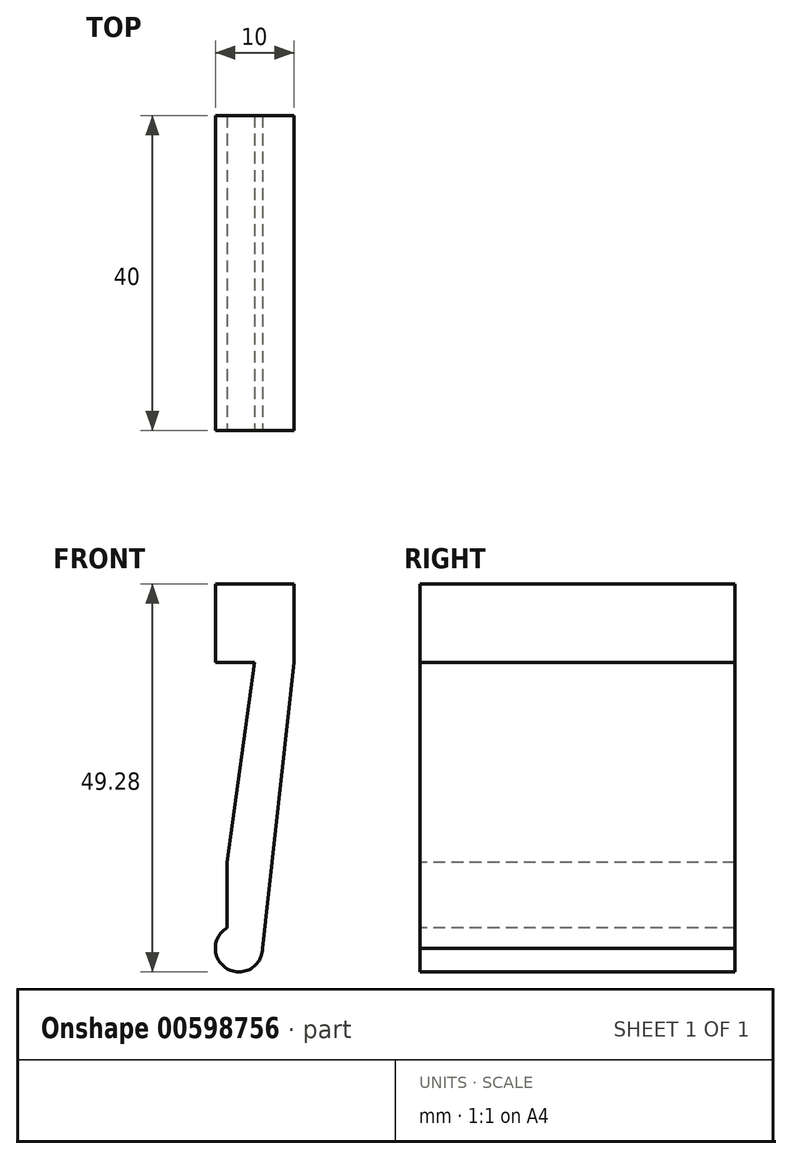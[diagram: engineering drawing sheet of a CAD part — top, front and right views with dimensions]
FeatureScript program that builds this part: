
annotation { "Feature Type Name" : "Feature", "Feature Type Description" : "" }
export const myFeature = defineFeature(function(context is Context, id is Id, definition is map)
    precondition{}
    {
        {
            var Q0;
            Q0=qCreatedBy(makeId("Front.planeOp"),FACE);
            var sketch = newSketch(context, id + "F0", { "sketchPlane" : qUnion([Q0])});
            skLineSegment(sketch, "E0.bottom", {"start": v(-5, 24.64) * mm, "end": v(5, 24.64) * mm});
            skLineSegment(sketch, "E0.top", {"start": v(-5, -24.64) * mm, "end": v(5, -24.64) * mm});
            skLineSegment(sketch, "E0.left", {"start": v(-5, 24.64) * mm, "end": v(-5, -24.64) * mm});
            skLineSegment(sketch, "E0.right", {"start": v(5, 24.64) * mm, "end": v(5, -24.64) * mm});
            skPoint(sketch, "E0.middle", {"position": v(0, 0) * mm});
            skSolve(sketch);
        }
        {
            var Q0;
            Q0=makeQuery(id+"F0.imprint","IMPRINT",FACE,{"disambiguationData":[TD([[makeQuery(id+"F0.imprint","IMPRINT",EDGE,{"derivedFrom":sQuery(id+"F0.wireOp",EDGE,"E0.bottom")}),-1.0]])]});
            extrude(context, id + "F1", {"entities" : qUnion([Q0]), "depth" : 40 * mm, "offsetDistance" : 25 * mm});
        }
        {
            var Q0;
            Q0=makeQuery(id+"F1.opExtrude","CAP_FACE",FACE,{"disambiguationData":[OSD([sQuery(id+"F0.wireOp",EDGE,"E0.bottom"),sQuery(id+"F0.wireOp",EDGE,"E0.top"),sQuery(id+"F0.wireOp",EDGE,"E0.left"),sQuery(id+"F0.wireOp",EDGE,"E0.right")])],"isStart":false});
            var sketch = newSketch(context, id + "F2", { "sketchPlane" : qUnion([Q0])});
            skLineSegment(sketch, "E1", {"start": v(-5, 24.64) * mm, "end": v(-5, 14.64) * mm});
            skFitSpline(sketch, "E2", {"points": [v(-5, 14.64) * mm, v(-5, -24.64) * mm], "startDerivative": vector(0, -39.28) * mm, "endDerivative": vector(0, -39.28) * mm});
            skLineSegment(sketch, "E3", {"start": v(-5, 14.64) * mm, "end": v(0, 14.64) * mm});
            skLineSegment(sketch, "E4", {"start": v(-5, -24.64) * mm, "end": v(-2, -24.64) * mm});
            skLineSegment(sketch, "E5", {"start": v(-2, -24.64) * mm, "end": v(-2, -21.64) * mm});
            skCircle(sketch, "E6", {"center": v(-2, -21.64) * mm, "radius": 3 * mm});
            skLineSegment(sketch, "E7", {"start": v(0, 14.64) * mm, "end": v(-2, -21.64) * mm});
            skLineSegment(sketch, "E8", {"start": v(-5, -21.64) * mm, "end": v(0, 14.64) * mm});
            skLineSegment(sketch, "E9", {"start": v(1, -21.64) * mm, "end": v(5, 14.64) * mm});
            skLineSegment(sketch, "E10", {"start": v(-3.5, -24.64) * mm, "end": v(-3.5, -10.76) * mm});
            skSolve(sketch);
        }
        {
            var Q0;
            {var subQ3=sQuery(id+"F2.wireOp",EDGE,"E9");Q0=makeQuery(id+"F2.imprint","IMPRINT",FACE,{"disambiguationData":[TD([[makeQuery(id+"F2.imprint","IMPRINT",EDGE,{"derivedFrom":subQ3}),-1.0]])]});}
            var Q1;
            {var subQ0=sQuery(id+"F2.wireOp",EDGE,"E4");Q1=makeQuery(id+"F2.imprint","IMPRINT",FACE,{"disambiguationData":[TD([[makeQuery(id+"F2.imprint","IMPRINT",EDGE,{"derivedFrom":subQ0}),1.0]])]});}
            var Q2;
            {var subQ0=sQuery(id+"F2.wireOp",EDGE,"E4");var subQ1=sQuery(id+"F2.wireOp",EDGE,"E2");var subQ2=makeQuery(id+"F2.imprint","INTERSECT",VERTEX,{"derivedFrom":[subQ1,subQ0]});Q2=makeQuery(id+"F2.imprint","IMPRINT",FACE,{"disambiguationData":[TD([[makeQuery(id+"F2.imprint","IMPRINT",EDGE,{"disambiguationData":[TD([[subQ2,-1.0]])],"derivedFrom":subQ0}),1.0]])]});}
            var Q3;
            {var subQ0=sQuery(id+"F2.wireOp",EDGE,"E10");var subQ1=sQuery(id+"F2.wireOp",EDGE,"E6");var subQ2=makeQuery(id+"F2.imprint","INTERSECT",VERTEX,{"disambiguationData":[OD(0.0)],"derivedFrom":[subQ1,subQ0]});Q3=makeQuery(id+"F2.imprint","IMPRINT",FACE,{"disambiguationData":[TD([[makeQuery(id+"F2.imprint","IMPRINT",EDGE,{"disambiguationData":[TD([[subQ2,-1.0]])],"derivedFrom":subQ1}),-1.0]])]});}
            var Q4;
            {var subQ6=sQuery(id+"F2.wireOp",EDGE,"E3");Q4=makeQuery(id+"F2.imprint","IMPRINT",FACE,{"disambiguationData":[TD([[makeQuery(id+"F2.imprint","IMPRINT",EDGE,{"derivedFrom":subQ6}),-1.0]])]});}
            extrude(context, id + "F3", {"entities" : qUnion([Q0, Q1, Q2, Q3, Q4]), "operationType" : NewBodyOperationType.REMOVE, "oppositeDirection" : true, "depth" : 40 * mm, "offsetDistance" : 25 * mm});
        }
    });
